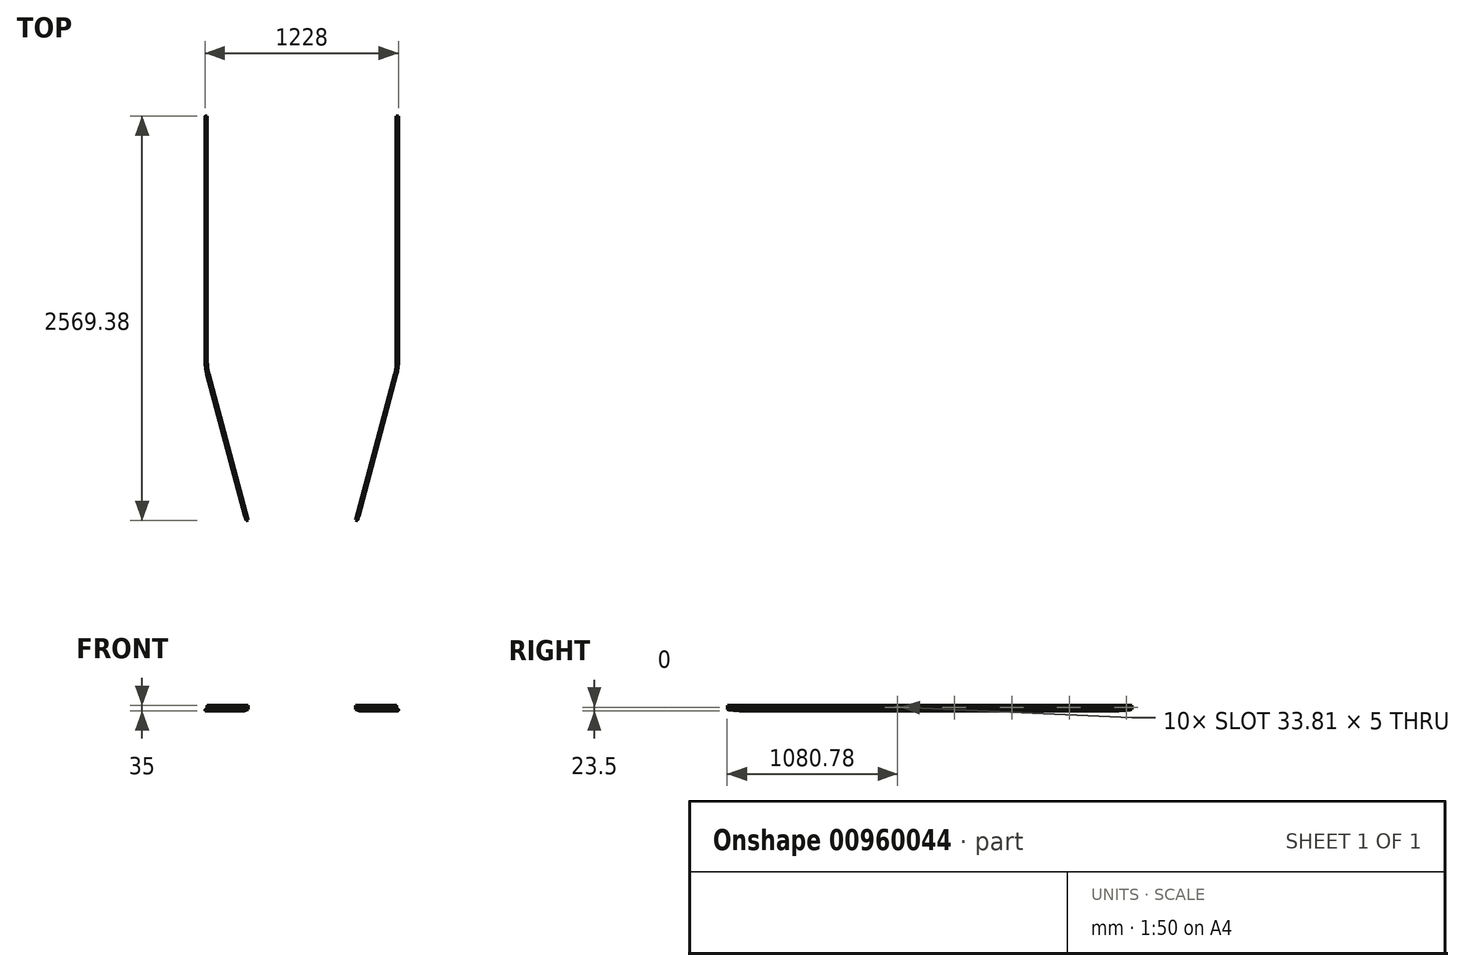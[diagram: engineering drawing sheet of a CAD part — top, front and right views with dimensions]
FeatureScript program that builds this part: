
annotation { "Feature Type Name" : "Feature", "Feature Type Description" : "" }
export const myFeature = defineFeature(function(context is Context, id is Id, definition is map)
    precondition{}
    {
        {
            var Q0;
            Q0=qCreatedBy(makeId("Front.planeOp"),FACE);
            var sketch = newSketch(context, id + "F0", { "sketchPlane" : qUnion([Q0])});
            skLineSegment(sketch, "E0.bottom", {"start": v(0, 0) * mm, "end": v(1.5, 0) * mm});
            skLineSegment(sketch, "E0.top", {"start": v(0, 35) * mm, "end": v(1.5, 35) * mm});
            skLineSegment(sketch, "E0.left", {"start": v(0, 0) * mm, "end": v(0, 35) * mm});
            skLineSegment(sketch, "E0.right", {"start": v(1.5, 12.5) * mm, "end": v(1.5, 35) * mm});
            skLineSegment(sketch, "E1.top", {"start": v(1.5, 12.5) * mm, "end": v(14, 12.5) * mm});
            skLineSegment(sketch, "E2", {"start": v(1.5, 0) * mm, "end": v(4.5, 0) * mm});
            skLineSegment(sketch, "E3", {"start": v(1.5, 12.5) * mm, "end": v(1.5, 0) * mm, "construction": true});
            skLineSegment(sketch, "E4", {"start": v(4.5, 0) * mm, "end": v(9.22, 0) * mm, "construction": true});
            skLineSegment(sketch, "E5", {"start": v(14, 12.5) * mm, "end": v(14, 0) * mm});
            skLineSegment(sketch, "E6", {"start": v(14, 0) * mm, "end": v(9.22, 0) * mm});
            skLineSegment(sketch, "E7", {"start": v(4.5, 0) * mm, "end": v(4.5, 1.5) * mm});
            skLineSegment(sketch, "E8", {"start": v(9.22, 0) * mm, "end": v(9.22, 1.5) * mm});
            skArc(sketch, "E9", {"start": v(9.22, 1.5) * mm, "mid": v(6.86, 10.9) * mm, "end": v(4.5, 1.5) * mm});
            skSolve(sketch);
        }
        {
            var Q0;
            Q0=qCreatedBy(makeId("Top.planeOp"),FACE);
            var sketch = newSketch(context, id + "F1", { "sketchPlane" : qUnion([Q0])});
            skLineSegment(sketch, "E10", {"start": v(0, 0) * mm, "end": v(0, -1560.5) * mm});
            skLineSegment(sketch, "E11", {"start": v(-10.22, -1638.15) * mm, "end": v(-258.82, -2565.93) * mm});
            skPoint(sketch, "E12.visualSharp", {"position": v(0, -1600) * mm});
            skArc(sketch, "E12.filletArc", {"start": v(-10.22, -1638.15) * mm, "mid": v(-2.57, -1599.66) * mm, "end": v(0, -1560.5) * mm});
            skSolve(sketch);
        }
        {
            var Q0;
            Q0=makeQuery(id+"F0.imprint","IMPRINT",FACE,{"disambiguationData":[TD([[makeQuery(id+"F0.imprint","IMPRINT",EDGE,{"derivedFrom":sQuery(id+"F0.wireOp",EDGE,"E0.bottom")}),1.0]])]});
            var Q1;
            Q1=sQuery(id+"F1.wireOp",EDGE,"E10");
            var Q2;
            Q2=sQuery(id+"F1.wireOp",EDGE,"E11");
            var Q3;
            Q3=sQuery(id+"F1.wireOp",EDGE,"E12.filletArc");
            sweep(context, id + "F2", {"profiles" : qUnion([Q0]), "path" : qUnion([Q1, Q2, Q3])});
        }
        {
            var Q0;
            Q0=makeQuery(id+"F2.opSweep","SWEPT_EDGE",EDGE,{"disambiguationData":[OSD([sQuery(id+"F0.wireOp",EDGE,"E1.top"),sQuery(id+"F0.wireOp",EDGE,"E5"),sQuery(id+"F1.wireOp",EDGE,"E11")])]});
            fillet(context, id + "F3", {"entities" : qUnion([Q0]), "radius" : 6.3 * mm, "tangentPropagation" : true, "allowEdgeOverflow" : false});
        }
        {
            var Q0;
            Q0=makeQuery(id+"F2.opSweep","SWEPT_EDGE",EDGE,{"disambiguationData":[OSD([sQuery(id+"F0.wireOp",EDGE,"E5"),sQuery(id+"F0.wireOp",EDGE,"E6"),sQuery(id+"F1.wireOp",EDGE,"E11")])]});
            fillet(context, id + "F4", {"entities" : qUnion([Q0]), "radius" : 5 * mm, "tangentPropagation" : true, "allowEdgeOverflow" : false});
        }
        {
            var Q0;
            Q0=makeQuery(id+"F2.opSweep","SWEPT_FACE",FACE,{"disambiguationData":[OSD([sQuery(id+"F0.wireOp",EDGE,"E0.right"),sQuery(id+"F1.wireOp",EDGE,"E11")])]});
            var sketch = newSketch(context, id + "F5", { "sketchPlane" : qUnion([Q0])});
            skLineSegment(sketch, "E13.bottom", {"start": v(-2520.48, 26) * mm, "end": v(-2485.48, 26) * mm});
            skLineSegment(sketch, "E13.top", {"start": v(-2520.48, 21) * mm, "end": v(-2485.48, 21) * mm});
            skLineSegment(sketch, "E13.left", {"start": v(-2520.48, 26) * mm, "end": v(-2520.48, 21) * mm});
            skLineSegment(sketch, "E13.right", {"start": v(-2485.48, 26) * mm, "end": v(-2485.48, 21) * mm});
            skLineSegment(sketch, "E14", {"start": v(-2485.48, 21) * mm, "end": v(-2095.48, 21) * mm, "construction": true});
            skLineSegment(sketch, "E15.bottom", {"start": v(-2095.48, 21) * mm, "end": v(-2060.48, 21) * mm});
            skLineSegment(sketch, "E15.top", {"start": v(-2095.48, 26) * mm, "end": v(-2060.48, 26) * mm});
            skLineSegment(sketch, "E15.left", {"start": v(-2095.48, 21) * mm, "end": v(-2095.48, 26) * mm});
            skLineSegment(sketch, "E15.right", {"start": v(-2060.48, 21) * mm, "end": v(-2060.48, 26) * mm});
            skLineSegment(sketch, "E16", {"start": v(-2060.48, 21) * mm, "end": v(-1670.48, 21) * mm, "construction": true});
            skLineSegment(sketch, "E17.bottom", {"start": v(-1670.48, 21) * mm, "end": v(-1635.48, 21) * mm});
            skLineSegment(sketch, "E17.top", {"start": v(-1670.48, 26) * mm, "end": v(-1635.48, 26) * mm});
            skLineSegment(sketch, "E17.left", {"start": v(-1670.48, 21) * mm, "end": v(-1670.48, 26) * mm});
            skLineSegment(sketch, "E17.right", {"start": v(-1635.48, 21) * mm, "end": v(-1635.48, 26) * mm});
            skSolve(sketch);
        }
        {
            var Q0;
            Q0 = qSketchRegion(id + "F5", true);
            extrude(context, id + "F6", {"entities" : qUnion([Q0]), "operationType" : NewBodyOperationType.REMOVE, "oppositeDirection" : true, "depth" : 25 * mm, "offsetDistance" : 25 * mm});
        }
        {
            var Q0;
            Q0=makeQuery(id+"F2.opSweep","SWEPT_FACE",FACE,{"disambiguationData":[OSD([sQuery(id+"F0.wireOp",EDGE,"E0.right"),sQuery(id+"F1.wireOp",EDGE,"E10")])]});
            var sketch = newSketch(context, id + "F7", { "sketchPlane" : qUnion([Q0])});
            skLineSegment(sketch, "E18.bottom", {"start": v(-1505.5, 26) * mm, "end": v(-1471.7, 26) * mm});
            skLineSegment(sketch, "E18.top", {"start": v(-1505.5, 21) * mm, "end": v(-1471.7, 21) * mm});
            skLineSegment(sketch, "E18.left", {"start": v(-1505.5, 26) * mm, "end": v(-1505.5, 21) * mm});
            skLineSegment(sketch, "E18.right", {"start": v(-1471.7, 26) * mm, "end": v(-1471.7, 21) * mm});
            skLineSegment(sketch, "E19", {"start": v(-1471.7, 21) * mm, "end": v(-1141.7, 21) * mm, "construction": true});
            skLineSegment(sketch, "E20.bottom", {"start": v(-1141.7, 21) * mm, "end": v(-1107.89, 21) * mm});
            skLineSegment(sketch, "E20.top", {"start": v(-1141.7, 26) * mm, "end": v(-1107.89, 26) * mm});
            skLineSegment(sketch, "E20.left", {"start": v(-1141.7, 21) * mm, "end": v(-1141.7, 26) * mm});
            skLineSegment(sketch, "E20.right", {"start": v(-1107.89, 21) * mm, "end": v(-1107.89, 26) * mm});
            skLineSegment(sketch, "E21", {"start": v(-1107.89, 21) * mm, "end": v(-777.89, 21) * mm, "construction": true});
            skLineSegment(sketch, "E22.bottom", {"start": v(-777.89, 21) * mm, "end": v(-744.08, 21) * mm});
            skLineSegment(sketch, "E22.top", {"start": v(-777.89, 26) * mm, "end": v(-744.08, 26) * mm});
            skLineSegment(sketch, "E22.left", {"start": v(-777.89, 21) * mm, "end": v(-777.89, 26) * mm});
            skLineSegment(sketch, "E22.right", {"start": v(-744.08, 21) * mm, "end": v(-744.08, 26) * mm});
            skLineSegment(sketch, "E23", {"start": v(-744.08, 21) * mm, "end": v(-414.08, 21) * mm, "construction": true});
            skLineSegment(sketch, "E24.bottom", {"start": v(-414.08, 21) * mm, "end": v(-380.27, 21) * mm});
            skLineSegment(sketch, "E24.top", {"start": v(-414.08, 26) * mm, "end": v(-380.27, 26) * mm});
            skLineSegment(sketch, "E24.left", {"start": v(-414.08, 21) * mm, "end": v(-414.08, 26) * mm});
            skLineSegment(sketch, "E24.right", {"start": v(-380.27, 21) * mm, "end": v(-380.27, 26) * mm});
            skLineSegment(sketch, "E25", {"start": v(-380.27, 21) * mm, "end": v(-50.27, 21) * mm, "construction": true});
            skLineSegment(sketch, "E26.bottom", {"start": v(-50.27, 21) * mm, "end": v(-16.47, 21) * mm});
            skLineSegment(sketch, "E26.top", {"start": v(-50.27, 26) * mm, "end": v(-16.47, 26) * mm});
            skLineSegment(sketch, "E26.left", {"start": v(-50.27, 21) * mm, "end": v(-50.27, 26) * mm});
            skLineSegment(sketch, "E26.right", {"start": v(-16.47, 21) * mm, "end": v(-16.47, 26) * mm});
            skSolve(sketch);
        }
        {
            var Q0;
            Q0 = qSketchRegion(id + "F7", true);
            extrude(context, id + "F8", {"entities" : qUnion([Q0]), "operationType" : NewBodyOperationType.REMOVE, "oppositeDirection" : true, "depth" : 25 * mm, "offsetDistance" : 25 * mm});
        }
        {
            var Q0;
            Q0=makeQuery(id+"F6.boolean.opBoolean","COPY",EDGE,{"derivedFrom":makeQuery(id+"F6.opExtrude","SWEPT_EDGE",EDGE,{"disambiguationData":[OSD([sQuery(id+"F5.wireOp",EDGE,"E13.bottom"),sQuery(id+"F5.wireOp",EDGE,"E13.left")])]})});
            var Q1;
            Q1=makeQuery(id+"F6.boolean.opBoolean","COPY",EDGE,{"derivedFrom":makeQuery(id+"F6.opExtrude","SWEPT_EDGE",EDGE,{"disambiguationData":[OSD([sQuery(id+"F5.wireOp",EDGE,"E13.top"),sQuery(id+"F5.wireOp",EDGE,"E13.left")])]})});
            var Q2;
            Q2=makeQuery(id+"F6.boolean.opBoolean","COPY",EDGE,{"derivedFrom":makeQuery(id+"F6.opExtrude","SWEPT_EDGE",EDGE,{"disambiguationData":[OSD([sQuery(id+"F5.wireOp",EDGE,"E13.bottom"),sQuery(id+"F5.wireOp",EDGE,"E13.right")])]})});
            var Q3;
            Q3=makeQuery(id+"F6.boolean.opBoolean","COPY",EDGE,{"derivedFrom":makeQuery(id+"F6.opExtrude","SWEPT_EDGE",EDGE,{"disambiguationData":[OSD([sQuery(id+"F5.wireOp",EDGE,"E13.top"),sQuery(id+"F5.wireOp",EDGE,"E13.right")])]})});
            fillet(context, id + "F9", {"entities" : qUnion([Q0, Q1, Q2, Q3]), "radius" : 2.5 * mm, "tangentPropagation" : true, "allowEdgeOverflow" : false});
        }
        {
            var Q0;
            Q0=makeQuery(id+"F6.boolean.opBoolean","COPY",EDGE,{"derivedFrom":makeQuery(id+"F6.opExtrude","SWEPT_EDGE",EDGE,{"disambiguationData":[OSD([sQuery(id+"F5.wireOp",EDGE,"E15.bottom"),sQuery(id+"F5.wireOp",EDGE,"E15.right")])]})});
            var Q1;
            Q1=makeQuery(id+"F6.boolean.opBoolean","COPY",EDGE,{"derivedFrom":makeQuery(id+"F6.opExtrude","SWEPT_EDGE",EDGE,{"disambiguationData":[OSD([sQuery(id+"F5.wireOp",EDGE,"E15.top"),sQuery(id+"F5.wireOp",EDGE,"E15.right")])]})});
            var Q2;
            Q2=makeQuery(id+"F6.boolean.opBoolean","COPY",EDGE,{"derivedFrom":makeQuery(id+"F6.opExtrude","SWEPT_EDGE",EDGE,{"disambiguationData":[OSD([sQuery(id+"F5.wireOp",EDGE,"E15.bottom"),sQuery(id+"F5.wireOp",EDGE,"E15.left")])]})});
            var Q3;
            Q3=makeQuery(id+"F6.boolean.opBoolean","COPY",EDGE,{"derivedFrom":makeQuery(id+"F6.opExtrude","SWEPT_EDGE",EDGE,{"disambiguationData":[OSD([sQuery(id+"F5.wireOp",EDGE,"E15.top"),sQuery(id+"F5.wireOp",EDGE,"E15.left")])]})});
            var Q4;
            Q4=makeQuery(id+"F6.boolean.opBoolean","COPY",EDGE,{"derivedFrom":makeQuery(id+"F6.opExtrude","SWEPT_EDGE",EDGE,{"disambiguationData":[OSD([sQuery(id+"F5.wireOp",EDGE,"E17.bottom"),sQuery(id+"F5.wireOp",EDGE,"E17.left")])]})});
            var Q5;
            Q5=makeQuery(id+"F6.boolean.opBoolean","COPY",EDGE,{"derivedFrom":makeQuery(id+"F6.opExtrude","SWEPT_EDGE",EDGE,{"disambiguationData":[OSD([sQuery(id+"F5.wireOp",EDGE,"E17.top"),sQuery(id+"F5.wireOp",EDGE,"E17.left")])]})});
            var Q6;
            Q6=makeQuery(id+"F6.boolean.opBoolean","COPY",EDGE,{"derivedFrom":makeQuery(id+"F6.opExtrude","SWEPT_EDGE",EDGE,{"disambiguationData":[OSD([sQuery(id+"F5.wireOp",EDGE,"E17.bottom"),sQuery(id+"F5.wireOp",EDGE,"E17.right")])]})});
            var Q7;
            Q7=makeQuery(id+"F6.boolean.opBoolean","COPY",EDGE,{"derivedFrom":makeQuery(id+"F6.opExtrude","SWEPT_EDGE",EDGE,{"disambiguationData":[OSD([sQuery(id+"F5.wireOp",EDGE,"E17.top"),sQuery(id+"F5.wireOp",EDGE,"E17.right")])]})});
            var Q8;
            Q8=makeQuery(id+"F8.boolean.opBoolean","COPY",EDGE,{"derivedFrom":makeQuery(id+"F8.opExtrude","SWEPT_EDGE",EDGE,{"disambiguationData":[OSD([sQuery(id+"F7.wireOp",EDGE,"E18.top"),sQuery(id+"F7.wireOp",EDGE,"E18.right")])]})});
            var Q9;
            Q9=makeQuery(id+"F8.boolean.opBoolean","COPY",EDGE,{"derivedFrom":makeQuery(id+"F8.opExtrude","SWEPT_EDGE",EDGE,{"disambiguationData":[OSD([sQuery(id+"F7.wireOp",EDGE,"E18.bottom"),sQuery(id+"F7.wireOp",EDGE,"E18.right")])]})});
            var Q10;
            Q10=makeQuery(id+"F8.boolean.opBoolean","COPY",EDGE,{"derivedFrom":makeQuery(id+"F8.opExtrude","SWEPT_EDGE",EDGE,{"disambiguationData":[OSD([sQuery(id+"F7.wireOp",EDGE,"E18.top"),sQuery(id+"F7.wireOp",EDGE,"E18.left")])]})});
            var Q11;
            Q11=makeQuery(id+"F8.boolean.opBoolean","COPY",EDGE,{"derivedFrom":makeQuery(id+"F8.opExtrude","SWEPT_EDGE",EDGE,{"disambiguationData":[OSD([sQuery(id+"F7.wireOp",EDGE,"E18.bottom"),sQuery(id+"F7.wireOp",EDGE,"E18.left")])]})});
            var Q12;
            Q12=makeQuery(id+"F8.boolean.opBoolean","COPY",EDGE,{"derivedFrom":makeQuery(id+"F8.opExtrude","SWEPT_EDGE",EDGE,{"disambiguationData":[OSD([sQuery(id+"F7.wireOp",EDGE,"E20.bottom"),sQuery(id+"F7.wireOp",EDGE,"E20.left")])]})});
            var Q13;
            Q13=makeQuery(id+"F8.boolean.opBoolean","COPY",EDGE,{"derivedFrom":makeQuery(id+"F8.opExtrude","SWEPT_EDGE",EDGE,{"disambiguationData":[OSD([sQuery(id+"F7.wireOp",EDGE,"E20.top"),sQuery(id+"F7.wireOp",EDGE,"E20.left")])]})});
            var Q14;
            Q14=makeQuery(id+"F8.boolean.opBoolean","COPY",EDGE,{"derivedFrom":makeQuery(id+"F8.opExtrude","SWEPT_EDGE",EDGE,{"disambiguationData":[OSD([sQuery(id+"F7.wireOp",EDGE,"E20.bottom"),sQuery(id+"F7.wireOp",EDGE,"E20.right")])]})});
            var Q15;
            Q15=makeQuery(id+"F8.boolean.opBoolean","COPY",EDGE,{"derivedFrom":makeQuery(id+"F8.opExtrude","SWEPT_EDGE",EDGE,{"disambiguationData":[OSD([sQuery(id+"F7.wireOp",EDGE,"E20.top"),sQuery(id+"F7.wireOp",EDGE,"E20.right")])]})});
            fillet(context, id + "F10", {"entities" : qUnion([Q0, Q1, Q2, Q3, Q4, Q5, Q6, Q7, Q8, Q9, Q10, Q11, Q12, Q13, Q14, Q15]), "radius" : 2.5 * mm, "tangentPropagation" : true, "allowEdgeOverflow" : false});
        }
        {
            var Q0;
            Q0=makeQuery(id+"F8.boolean.opBoolean","COPY",EDGE,{"derivedFrom":makeQuery(id+"F8.opExtrude","SWEPT_EDGE",EDGE,{"disambiguationData":[OSD([sQuery(id+"F7.wireOp",EDGE,"E22.bottom"),sQuery(id+"F7.wireOp",EDGE,"E22.right")])]})});
            var Q1;
            Q1=makeQuery(id+"F8.boolean.opBoolean","COPY",EDGE,{"derivedFrom":makeQuery(id+"F8.opExtrude","SWEPT_EDGE",EDGE,{"disambiguationData":[OSD([sQuery(id+"F7.wireOp",EDGE,"E22.top"),sQuery(id+"F7.wireOp",EDGE,"E22.right")])]})});
            var Q2;
            Q2=makeQuery(id+"F8.boolean.opBoolean","COPY",EDGE,{"derivedFrom":makeQuery(id+"F8.opExtrude","SWEPT_EDGE",EDGE,{"disambiguationData":[OSD([sQuery(id+"F7.wireOp",EDGE,"E22.bottom"),sQuery(id+"F7.wireOp",EDGE,"E22.left")])]})});
            var Q3;
            Q3=makeQuery(id+"F8.boolean.opBoolean","COPY",EDGE,{"derivedFrom":makeQuery(id+"F8.opExtrude","SWEPT_EDGE",EDGE,{"disambiguationData":[OSD([sQuery(id+"F7.wireOp",EDGE,"E22.top"),sQuery(id+"F7.wireOp",EDGE,"E22.left")])]})});
            var Q4;
            Q4=makeQuery(id+"F8.boolean.opBoolean","COPY",EDGE,{"derivedFrom":makeQuery(id+"F8.opExtrude","SWEPT_EDGE",EDGE,{"disambiguationData":[OSD([sQuery(id+"F7.wireOp",EDGE,"E24.bottom"),sQuery(id+"F7.wireOp",EDGE,"E24.right")])]})});
            var Q5;
            Q5=makeQuery(id+"F8.boolean.opBoolean","COPY",EDGE,{"derivedFrom":makeQuery(id+"F8.opExtrude","SWEPT_EDGE",EDGE,{"disambiguationData":[OSD([sQuery(id+"F7.wireOp",EDGE,"E24.top"),sQuery(id+"F7.wireOp",EDGE,"E24.right")])]})});
            var Q6;
            Q6=makeQuery(id+"F8.boolean.opBoolean","COPY",EDGE,{"derivedFrom":makeQuery(id+"F8.opExtrude","SWEPT_EDGE",EDGE,{"disambiguationData":[OSD([sQuery(id+"F7.wireOp",EDGE,"E24.bottom"),sQuery(id+"F7.wireOp",EDGE,"E24.left")])]})});
            var Q7;
            Q7=makeQuery(id+"F8.boolean.opBoolean","COPY",EDGE,{"derivedFrom":makeQuery(id+"F8.opExtrude","SWEPT_EDGE",EDGE,{"disambiguationData":[OSD([sQuery(id+"F7.wireOp",EDGE,"E24.top"),sQuery(id+"F7.wireOp",EDGE,"E24.left")])]})});
            var Q8;
            Q8=makeQuery(id+"F8.boolean.opBoolean","COPY",EDGE,{"derivedFrom":makeQuery(id+"F8.opExtrude","SWEPT_EDGE",EDGE,{"disambiguationData":[OSD([sQuery(id+"F7.wireOp",EDGE,"E26.bottom"),sQuery(id+"F7.wireOp",EDGE,"E26.right")])]})});
            var Q9;
            Q9=makeQuery(id+"F8.boolean.opBoolean","COPY",EDGE,{"derivedFrom":makeQuery(id+"F8.opExtrude","SWEPT_EDGE",EDGE,{"disambiguationData":[OSD([sQuery(id+"F7.wireOp",EDGE,"E26.top"),sQuery(id+"F7.wireOp",EDGE,"E26.right")])]})});
            var Q10;
            Q10=makeQuery(id+"F8.boolean.opBoolean","COPY",EDGE,{"derivedFrom":makeQuery(id+"F8.opExtrude","SWEPT_EDGE",EDGE,{"disambiguationData":[OSD([sQuery(id+"F7.wireOp",EDGE,"E26.bottom"),sQuery(id+"F7.wireOp",EDGE,"E26.left")])]})});
            var Q11;
            Q11=makeQuery(id+"F8.boolean.opBoolean","COPY",EDGE,{"derivedFrom":makeQuery(id+"F8.opExtrude","SWEPT_EDGE",EDGE,{"disambiguationData":[OSD([sQuery(id+"F7.wireOp",EDGE,"E26.top"),sQuery(id+"F7.wireOp",EDGE,"E26.left")])]})});
            fillet(context, id + "F11", {"entities" : qUnion([Q0, Q1, Q2, Q3, Q4, Q5, Q6, Q7, Q8, Q9, Q10, Q11]), "radius" : 2.5 * mm, "tangentPropagation" : true, "allowEdgeOverflow" : false});
        }
        {
            var Q0;
            Q0=makeQuery(id+"F2.opSweep","SWEPT_FACE",FACE,{"disambiguationData":[OSD([sQuery(id+"F0.wireOp",EDGE,"E0.left"),sQuery(id+"F1.wireOp",EDGE,"E11")])]});
            var sketch = newSketch(context, id + "F12", { "sketchPlane" : qUnion([Q0])});
            skLineSegment(sketch, "E27", {"start": v(2545.48, 0) * mm, "end": v(2545.48, 9) * mm});
            skLineSegment(sketch, "E28", {"start": v(2545.48, 9) * mm, "end": v(2445.48, 0) * mm});
            skLineSegment(sketch, "E29", {"start": v(2545.48, 0) * mm, "end": v(2445.48, 0) * mm});
            skSolve(sketch);
        }
        {
            var Q0;
            Q0 = qSketchRegion(id + "F12", true);
            extrude(context, id + "F13", {"entities" : qUnion([Q0]), "operationType" : NewBodyOperationType.REMOVE, "oppositeDirection" : true, "depth" : 25 * mm, "offsetDistance" : 25 * mm});
        }
        {
            var Q0;
            Q0=makeQuery(id+"F2.opSweep","SWEPT_FACE",FACE,{"disambiguationData":[OSD([sQuery(id+"F0.wireOp",EDGE,"E0.left"),sQuery(id+"F1.wireOp",EDGE,"E10")])]});
            var sketch = newSketch(context, id + "F14", { "sketchPlane" : qUnion([Q0])});
            skLineSegment(sketch, "E30", {"start": v(0, 0) * mm, "end": v(0, 9) * mm});
            skLineSegment(sketch, "E31", {"start": v(0, 9) * mm, "end": v(100, 0) * mm});
            skLineSegment(sketch, "E32", {"start": v(100, 0) * mm, "end": v(0, 0) * mm});
            skSolve(sketch);
        }
        {
            var Q0;
            Q0 = qSketchRegion(id + "F14", true);
            extrude(context, id + "F15", {"entities" : qUnion([Q0]), "operationType" : NewBodyOperationType.REMOVE, "oppositeDirection" : true, "depth" : 25 * mm, "offsetDistance" : 25 * mm});
        }
        {
            var Q0;
            Q0=qCreatedBy(makeId("Right.planeOp"),FACE);
            cPlane(context, id + "F16", {"entities" : qUnion([Q0]), "cplaneType" : CPlaneType.OFFSET, "offset" : 600 * mm, "oppositeDirection" : true, "width" : 150 * mm, "height" : 150 * mm});
        }
        {
            var Q0;
            Q0=makeQuery(id+"F2.opSweep","SWEPT_BODY",BODY,{"disambiguationData":[OSD([sQuery(id+"F0.wireOp",EDGE,"E0.bottom"),sQuery(id+"F0.wireOp",EDGE,"E0.top"),sQuery(id+"F0.wireOp",EDGE,"E0.left"),sQuery(id+"F0.wireOp",EDGE,"E0.right"),sQuery(id+"F0.wireOp",EDGE,"E1.top"),sQuery(id+"F0.wireOp",EDGE,"E2"),sQuery(id+"F0.wireOp",EDGE,"E5"),sQuery(id+"F0.wireOp",EDGE,"E6"),sQuery(id+"F0.wireOp",EDGE,"E7"),sQuery(id+"F0.wireOp",EDGE,"E8"),sQuery(id+"F0.wireOp",EDGE,"E9"),sQuery(id+"F1.wireOp",EDGE,"E10")])]});
            var Q1;
            Q1=qCreatedBy(id+"F16.planeOp",FACE);
            mirror(context, id + "F17", {"operationType" : NewBodyOperationType.ADD, "entities" : qUnion([Q0]), "mirrorPlane" : qUnion([Q1])});
        }
    });
